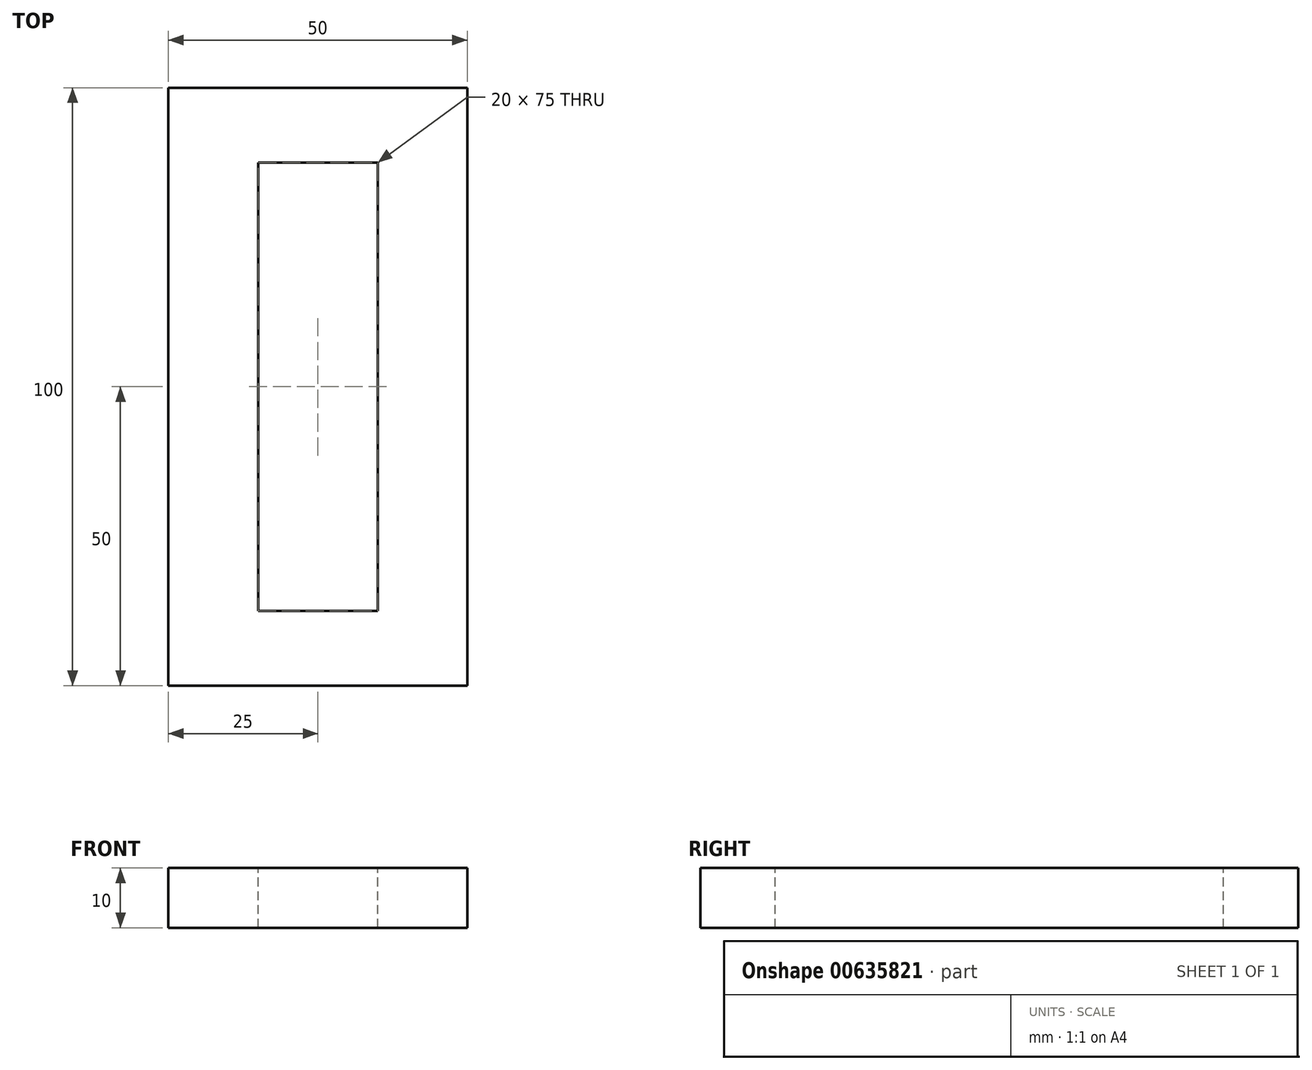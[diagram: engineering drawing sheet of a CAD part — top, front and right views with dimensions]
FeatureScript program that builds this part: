
annotation { "Feature Type Name" : "Feature", "Feature Type Description" : "" }
export const myFeature = defineFeature(function(context is Context, id is Id, definition is map)
    precondition{}
    {
        {
            var Q0;
            Q0=qCreatedBy(makeId("Top.planeOp"),FACE);
            var sketch = newSketch(context, id + "F0", { "sketchPlane" : qUnion([Q0])});
            skLineSegment(sketch, "E0.bottom", {"start": v(-25, 50) * mm, "end": v(25, 50) * mm});
            skLineSegment(sketch, "E0.top", {"start": v(-25, -50) * mm, "end": v(25, -50) * mm});
            skLineSegment(sketch, "E0.left", {"start": v(-25, 50) * mm, "end": v(-25, -50) * mm});
            skLineSegment(sketch, "E0.right", {"start": v(25, 50) * mm, "end": v(25, -50) * mm});
            skPoint(sketch, "E0.middle", {"position": v(0, 0) * mm});
            skSolve(sketch);
        }
        {
            var Q0;
            Q0=makeQuery(id+"F0.imprint","IMPRINT",FACE,{"disambiguationData":[TD([[makeQuery(id+"F0.imprint","IMPRINT",EDGE,{"derivedFrom":sQuery(id+"F0.wireOp",EDGE,"E0.bottom")}),-1.0]])]});
            extrude(context, id + "F1", {"entities" : qUnion([Q0]), "depth" : 10 * mm, "offsetDistance" : 25 * mm});
        }
        {
            var Q0;
            Q0=makeQuery(id+"F1.opExtrude","CAP_FACE",FACE,{"disambiguationData":[OSD([sQuery(id+"F0.wireOp",EDGE,"E0.bottom"),sQuery(id+"F0.wireOp",EDGE,"E0.top"),sQuery(id+"F0.wireOp",EDGE,"E0.left"),sQuery(id+"F0.wireOp",EDGE,"E0.right")])],"isStart":false});
            var sketch = newSketch(context, id + "F2", { "sketchPlane" : qUnion([Q0])});
            skLineSegment(sketch, "E1.bottom", {"start": v(-10, 37.5) * mm, "end": v(10, 37.5) * mm});
            skLineSegment(sketch, "E1.top", {"start": v(-10, -37.5) * mm, "end": v(10, -37.5) * mm});
            skLineSegment(sketch, "E1.left", {"start": v(-10, 37.5) * mm, "end": v(-10, -37.5) * mm});
            skLineSegment(sketch, "E1.right", {"start": v(10, 37.5) * mm, "end": v(10, -37.5) * mm});
            skPoint(sketch, "E1.middle", {"position": v(0, 0) * mm});
            skSolve(sketch);
        }
        {
            var Q0;
            Q0=makeQuery(id+"F2.imprint","IMPRINT",FACE,{"disambiguationData":[TD([[makeQuery(id+"F2.imprint","IMPRINT",EDGE,{"derivedFrom":sQuery(id+"F2.wireOp",EDGE,"E1.bottom")}),-1.0]])]});
            extrude(context, id + "F3", {"entities" : qUnion([Q0]), "operationType" : NewBodyOperationType.REMOVE, "endBound" : BoundingType.THROUGH_ALL, "oppositeDirection" : true, "depth" : 25 * mm, "offsetDistance" : 25 * mm});
        }
    });
